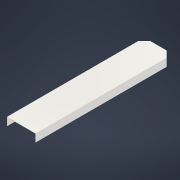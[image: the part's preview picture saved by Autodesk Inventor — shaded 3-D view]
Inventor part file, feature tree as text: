
AUTODESK INVENTOR PART (.ipt)
format: ipt  version: 2022 (Build 260153000, 153)  size: 135,680 bytes
history: native  units: mm
features: extrude x2, sketch x2, other x1, projected_geometry x1
ambient origin geometry x8: Origin, YZ Plane, XZ Plane, XY Plane, X Axis, Y Axis, Z Axis, Center Point
bodies: Body1 (feature_tree)
feature tree (6):
  other  "Sólido1"
  extrude  "Extrusión1"  Depth=230.0mm
  extrude  "Extrusión2"  Depth=60.0mm
  sketch  "Boceto1"  dims[d0=1100.0mm d1=230.0mm]
  sketch  "Boceto2"  dims[d2=50.0mm d3=50.0mm d4=50.0mm d5=50.0mm d6=3.0mm d7=0.0mm d8=2.5mm d9=60.0mm d10=0.0mm d11=30.0mm d12=30.0mm d13=300.0mm d14=500.0mm d15=100.0mm d16=100.0mm]
  projected_geometry  "Contorno proyectado1"
